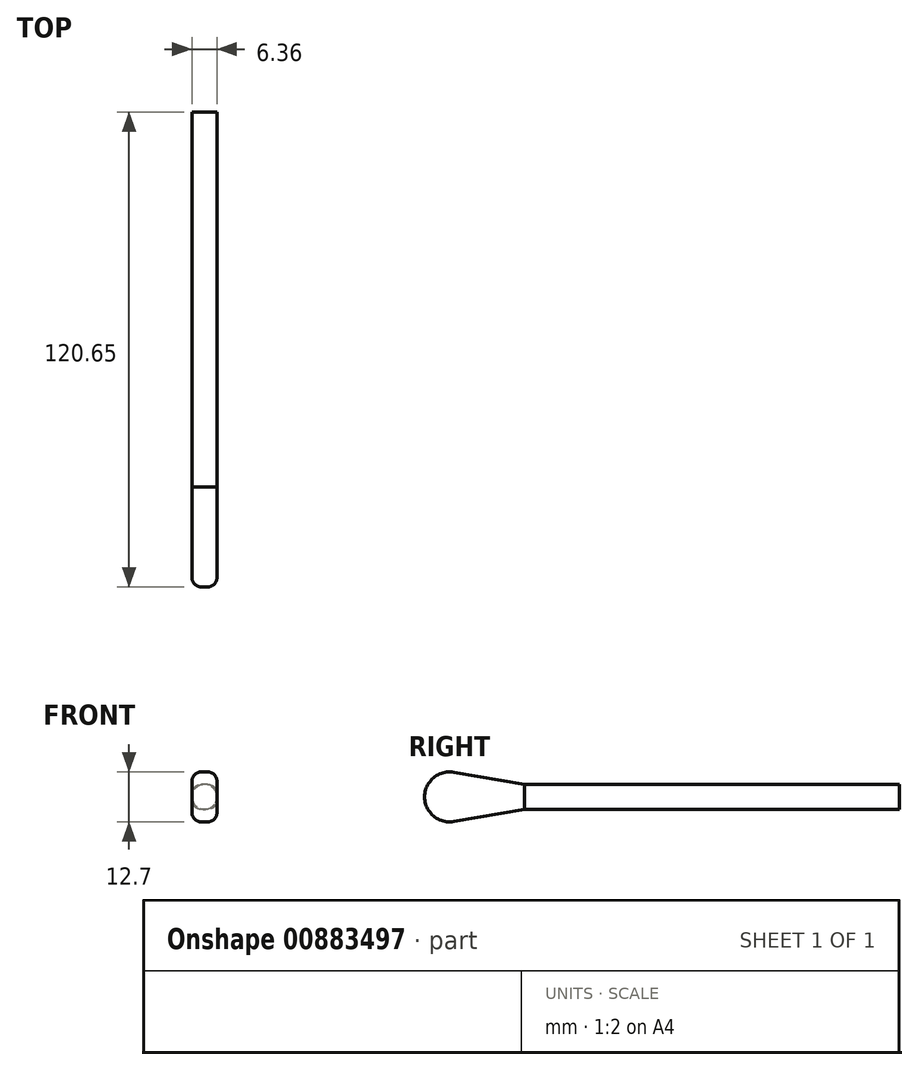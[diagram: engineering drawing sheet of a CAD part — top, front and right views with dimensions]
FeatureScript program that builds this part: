
annotation { "Feature Type Name" : "Feature", "Feature Type Description" : "" }
export const myFeature = defineFeature(function(context is Context, id is Id, definition is map)
    precondition{}
    {
        {
            var Q0;
            Q0=qCreatedBy(makeId("Front.planeOp"),FACE);
            var sketch = newSketch(context, id + "F0", { "sketchPlane" : qUnion([Q0])});
            skCircle(sketch, "E0", {"center": v(0, 0) * mm, "radius": 3.18 * mm});
            skSolve(sketch);
        }
        {
            var Q0;
            Q0=makeQuery(id+"F0.imprint","IMPRINT",FACE,{"disambiguationData":[TD([[makeQuery(id+"F0.imprint","IMPRINT",EDGE,{"derivedFrom":sQuery(id+"F0.wireOp",EDGE,"E0")}),1.0]])]});
            extrude(context, id + "F1", {"entities" : qUnion([Q0]), "endBound" : BoundingType.SYMMETRIC, "depth" : 101.6 * mm, "offsetDistance" : 25.4 * mm});
        }
        {
            var Q0;
            Q0=qCreatedBy(makeId("Right.planeOp"),FACE);
            var sketch = newSketch(context, id + "F2", { "sketchPlane" : qUnion([Q0])});
            skLineSegment(sketch, "E1", {"start": v(-44.45, 3.18) * mm, "end": v(-62.43, 6.26) * mm});
            skLineSegment(sketch, "E2", {"start": v(-44.45, -3.18) * mm, "end": v(-62.43, -6.26) * mm});
            skArc(sketch, "E3", {"start": v(-62.43, 6.26) * mm, "mid": v(-69.85, 0) * mm, "end": v(-62.43, -6.26) * mm});
            skLineSegment(sketch, "E4", {"start": v(-44.45, 3.18) * mm, "end": v(-44.45, -3.18) * mm});
            skLineSegment(sketch, "E5", {"start": v(-50.8, 3.18) * mm, "end": v(50.8, 3.18) * mm, "construction": true});
            skLineSegment(sketch, "E6", {"start": v(50.8, -3.18) * mm, "end": v(-50.8, -3.18) * mm, "construction": true});
            skLineSegment(sketch, "E7", {"start": v(-44.45, 0) * mm, "end": v(-63.5, 0) * mm, "construction": true});
            skSolve(sketch);
        }
        {
            var Q0;
            Q0 = qSketchRegion(id + "F2", true);
            extrude(context, id + "F3", {"entities" : qUnion([Q0]), "operationType" : NewBodyOperationType.ADD, "endBound" : BoundingType.SYMMETRIC, "depth" : 6.35 * mm, "offsetDistance" : 25.4 * mm});
        }
        {
            var Q0;
            Q0=makeQuery(id+"F3.opExtrude","CAP_EDGE",EDGE,{"disambiguationData":[OSD([sQuery(id+"F2.wireOp",EDGE,"E3")])],"isStart":false});
            var Q1;
            Q1=makeQuery(id+"F3.opExtrude","CAP_EDGE",EDGE,{"disambiguationData":[OSD([sQuery(id+"F2.wireOp",EDGE,"E3")])],"isStart":true});
            fillet(context, id + "F4", {"entities" : qUnion([Q0, Q1]), "radius" : 2.4 * mm, "tangentPropagation" : true, "allowEdgeOverflow" : false});
        }
    });
